# Revit family: Building-IEC309Connections-GEWISS-67IB-INTERLOCKED-SOCKET-OUTLETS_IP67_WITHOUT_BOTTOM_24V
name_source: partatom
category: Apparecchi elettrici
units: mm (PartAtom-declared; Revit-internal decimal feet)

## family parameters
Condiviso = Sì
Host = Superficie
Mantenere orientamento annotazione = Sì
Punto di calcolo locali = Sì
Quota connettore circolare = Usa diametro
Taglio con vuoti quando caricato = Sì
Tipo di parte = Normale

## types (1)
- GW66359N -  160VA 2P 230/24V V.INT.SOCK.O.N.B.SBF
    Catalogue = BUILDING
    Colour: = Violet
    Corpo presa = Light Blue
    Descrizione = 160VA 2P 230/24V V.INT.SOCK.O.N.B.SBF
    Electrocod = 2222
    Frequency = 50Hz
    Glow wire test: = 850 °C
    IDF = d0a0e1f0-d297-4b0e-81e3-45a49ddc2956
    IDT = 71bc45dc67804a6f91b0e4192ede9dae
    IP degree = IP67
    Immagine tipo = <Nessuno>
    Modello = GW66359N
    No. of poles = 2P
    Operating temperature: = -25 +40 °C
    Output voltage = 20-25 V
    Produttore = GEWISS S.p.A.
    Prospetto di default = 1219 mm
    Protection = Safety transformer
    Rated current (A) = 16
    Rated power = 160VA
    SEO = Socket outlet
    Shock resistance = IK08
    Simbolo presa = PRESAINDSTAGNA : 3P
    Struttura = Grigio RAL - 7035
    T1 = 230V
    T2 = 24V
    Technical sheet = https://www.gewiss.com
    Thermo-pressure with ball = 125
    Typology = Vertical
    URL = https://www.gewiss.com
    Version file RFA = 21.8
    With back-mounting box = No
    giallo = 0 mm  [stored 0 ft]
    presa = Grigio RAL - 7035

note: source unit labels omitted for Thermo-pressure with ball — the stored unit's dimension contradicts the parameter name (converter mislabeling)

note: [stored X ft] marks values corroborated as IEEE doubles in the binary element streams (Revit-internal decimal feet)

## geometry (parser evidence)
native form markers: Sweep x5
no freeform markers — native parametric forms only
